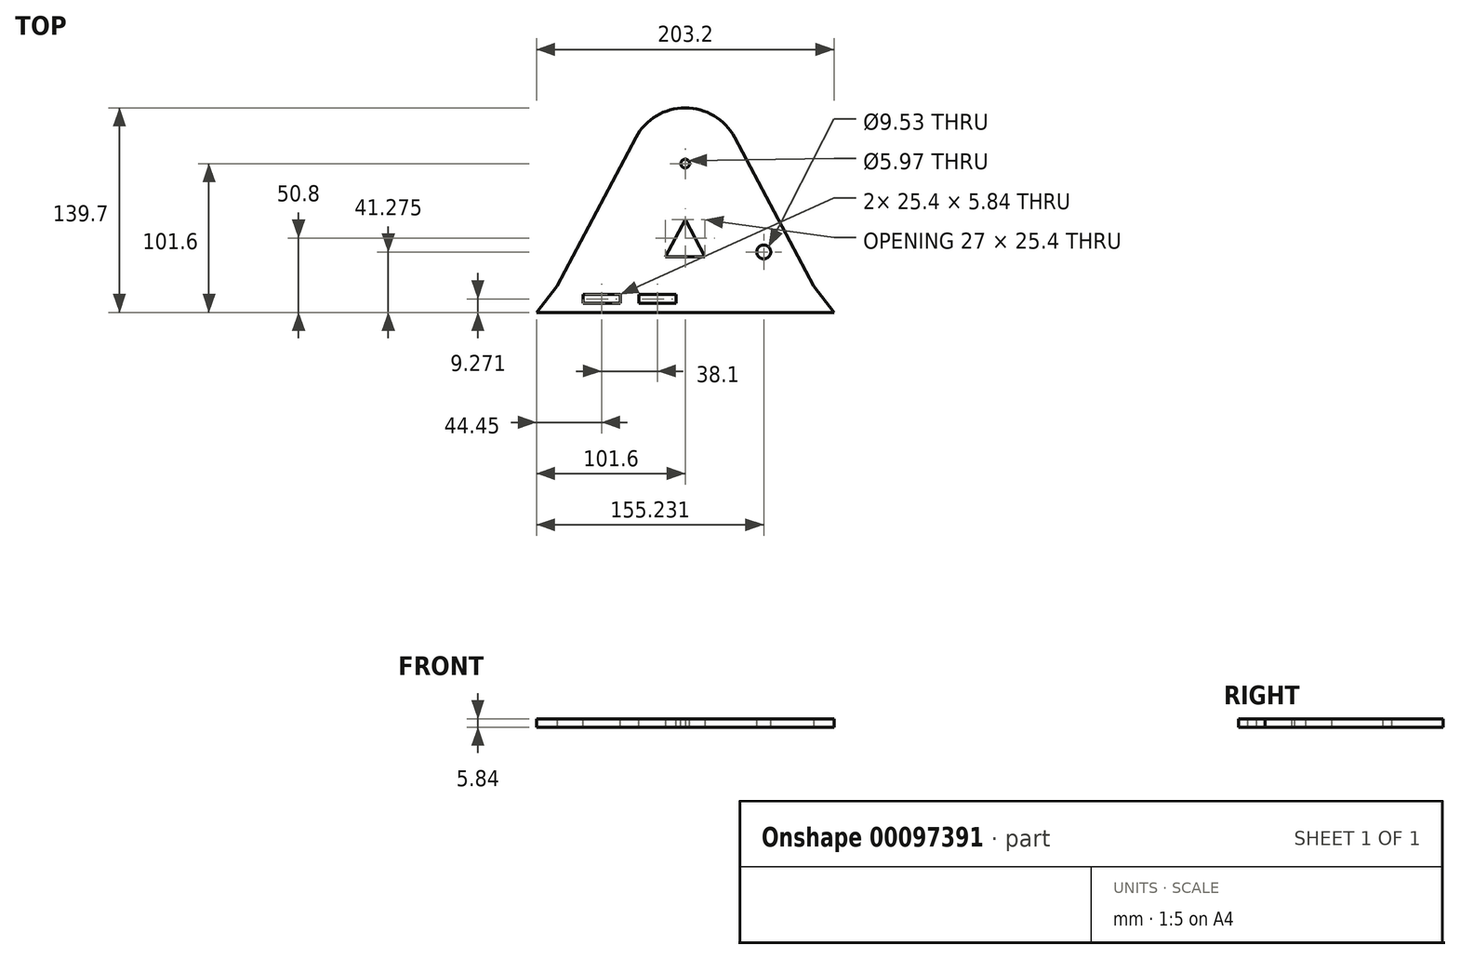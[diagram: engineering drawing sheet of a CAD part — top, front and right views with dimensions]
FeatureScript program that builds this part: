
annotation { "Feature Type Name" : "Feature", "Feature Type Description" : "" }
export const myFeature = defineFeature(function(context is Context, id is Id, definition is map)
    precondition{}
    {
        {
            var Q0;
            Q0=qCreatedBy(makeId("Top.planeOp"),FACE);
            var sketch = newSketch(context, id + "F0", { "sketchPlane" : qUnion([Q0])});
            skCircle(sketch, "E0", {"center": v(0, 0) * mm, "radius": 38.1 * mm});
            skCircle(sketch, "E1", {"center": v(54, -101.6) * mm, "radius": 38.1 * mm, "construction": true});
            skCircle(sketch, "E2", {"center": v(-54, -101.6) * mm, "radius": 38.1 * mm, "construction": true});
            skLineSegment(sketch, "E3", {"start": v(-87.64, -83.72) * mm, "end": v(-33.64, 17.88) * mm});
            skLineSegment(sketch, "E4", {"start": v(87.64, -83.72) * mm, "end": v(33.64, 17.88) * mm});
            skLineSegment(sketch, "E5", {"start": v(0, 0) * mm, "end": v(0, -101.6) * mm, "construction": true});
            skLineSegment(sketch, "E6", {"start": v(-54, -101.6) * mm, "end": v(54, -101.6) * mm, "construction": true});
            skLineSegment(sketch, "E7", {"start": v(-87.64, -83.72) * mm, "end": v(-101.6, -101.6) * mm});
            skLineSegment(sketch, "E8", {"start": v(-54, -101.6) * mm, "end": v(-101.6, -101.6) * mm});
            skLineSegment(sketch, "E9", {"start": v(87.64, -83.72) * mm, "end": v(101.6, -101.6) * mm});
            skLineSegment(sketch, "E10", {"start": v(54, -101.6) * mm, "end": v(101.6, -101.6) * mm});
            skLineSegment(sketch, "E11", {"start": v(0, -38.1) * mm, "end": v(-22.42, -80.28) * mm});
            skLineSegment(sketch, "E12", {"start": v(0, -38.1) * mm, "end": v(22.42, -80.28) * mm});
            skLineSegment(sketch, "E13", {"start": v(-22.42, -80.28) * mm, "end": v(22.42, -80.28) * mm});
            skLineSegment(sketch, "E14", {"start": v(54, -101.6) * mm, "end": v(-54, -101.6) * mm});
            skLineSegment(sketch, "E15", {"start": v(-54, -63.5) * mm, "end": v(54, -63.5) * mm});
            skLineSegment(sketch, "E16", {"start": v(13.5, -63.5) * mm, "end": v(13.5, -101.6) * mm, "construction": true});
            skLineSegment(sketch, "E17", {"start": v(13.5, -63.5) * mm, "end": v(76.9, -63.5) * mm, "construction": true});
            skSolve(sketch);
        }
        {
            var Q0;
            {var subQ0=sQuery(id+"F0.wireOp",EDGE,"E0");var subQ1=makeQuery(id+"F0.imprint","INTERSECT",VERTEX,{"derivedFrom":[subQ0,sQuery(id+"F0.wireOp",EDGE,"E3")]});Q0=makeQuery(id+"F0.imprint","IMPRINT",FACE,{"disambiguationData":[TD([[makeQuery(id+"F0.imprint","IMPRINT",EDGE,{"disambiguationData":[TD([[subQ1,1.0]])],"derivedFrom":subQ0}),1.0]])]});}
            var Q1;
            {var subQ0=sQuery(id+"F0.wireOp",EDGE,"E3");Q1=makeQuery(id+"F0.imprint","IMPRINT",FACE,{"disambiguationData":[TD([[makeQuery(id+"F0.imprint","IMPRINT",EDGE,{"derivedFrom":subQ0}),-1.0]])]});}
            var Q2;
            {var subQ0=sQuery(id+"F0.wireOp",EDGE,"E13");Q2=makeQuery(id+"F0.imprint","IMPRINT",FACE,{"disambiguationData":[TD([[makeQuery(id+"F0.imprint","IMPRINT",EDGE,{"derivedFrom":subQ0}),1.0]])]});}
            extrude(context, id + "F1", {"entities" : qUnion([Q0, Q1, Q2]), "depth" : 5.84 * mm});
        }
        {
            var Q0;
            Q0=makeQuery(id+"F1.opExtrude","CAP_FACE",FACE,{"disambiguationData":[OSD([sQuery(id+"F0.wireOp",EDGE,"E0"),sQuery(id+"F0.wireOp",EDGE,"E3"),sQuery(id+"F0.wireOp",EDGE,"E4"),sQuery(id+"F0.wireOp",EDGE,"E7"),sQuery(id+"F0.wireOp",EDGE,"E8"),sQuery(id+"F0.wireOp",EDGE,"E9"),sQuery(id+"F0.wireOp",EDGE,"E10"),sQuery(id+"F0.wireOp",EDGE,"E11"),sQuery(id+"F0.wireOp",EDGE,"E12"),sQuery(id+"F0.wireOp",EDGE,"E14"),sQuery(id+"F0.wireOp",EDGE,"E15")])],"isStart":false});
            var sketch = newSketch(context, id + "F2", { "sketchPlane" : qUnion([Q0])});
            skCircle(sketch, "E18", {"center": v(0, 0) * mm, "radius": 2.98 * mm});
            skCircle(sketch, "E19", {"center": v(53.63, -60.33) * mm, "radius": 4.76 * mm});
            skLineSegment(sketch, "E20", {"start": v(53.63, -60.33) * mm, "end": v(70.45, -51.39) * mm, "construction": true});
            skSolve(sketch);
        }
        {
            var Q0;
            Q0=makeQuery(id+"F2.imprint","IMPRINT",FACE,{"disambiguationData":[TD([[makeQuery(id+"F2.imprint","IMPRINT",EDGE,{"derivedFrom":sQuery(id+"F2.wireOp",EDGE,"E18")}),1.0]])]});
            var Q1;
            Q1=makeQuery(id+"F2.imprint","IMPRINT",FACE,{"disambiguationData":[TD([[makeQuery(id+"F2.imprint","IMPRINT",EDGE,{"derivedFrom":sQuery(id+"F2.wireOp",EDGE,"E19")}),1.0]])]});
            extrude(context, id + "F3", {"entities" : qUnion([Q0, Q1]), "operationType" : NewBodyOperationType.REMOVE, "oppositeDirection" : true, "depth" : 25.4 * mm});
        }
        {
            var Q0;
            Q0=makeQuery(id+"F1.opExtrude","CAP_FACE",FACE,{"disambiguationData":[OSD([sQuery(id+"F0.wireOp",EDGE,"E0"),sQuery(id+"F0.wireOp",EDGE,"E3"),sQuery(id+"F0.wireOp",EDGE,"E4"),sQuery(id+"F0.wireOp",EDGE,"E7"),sQuery(id+"F0.wireOp",EDGE,"E8"),sQuery(id+"F0.wireOp",EDGE,"E9"),sQuery(id+"F0.wireOp",EDGE,"E10"),sQuery(id+"F0.wireOp",EDGE,"E11"),sQuery(id+"F0.wireOp",EDGE,"E12"),sQuery(id+"F0.wireOp",EDGE,"E14"),sQuery(id+"F0.wireOp",EDGE,"E15")])],"isStart":false});
            var sketch = newSketch(context, id + "F4", { "sketchPlane" : qUnion([Q0])});
            skLineSegment(sketch, "E21.bottom", {"start": v(-6.35, -95.25) * mm, "end": v(-31.75, -95.25) * mm});
            skLineSegment(sketch, "E21.top", {"start": v(-6.35, -89.4) * mm, "end": v(-31.75, -89.4) * mm});
            skLineSegment(sketch, "E21.left", {"start": v(-6.35, -95.25) * mm, "end": v(-6.35, -89.4) * mm});
            skLineSegment(sketch, "E21.right", {"start": v(-31.75, -95.25) * mm, "end": v(-31.75, -89.4) * mm});
            skLineSegment(sketch, "E22.bottom", {"start": v(-44.45, -95.25) * mm, "end": v(-69.85, -95.25) * mm});
            skLineSegment(sketch, "E22.top", {"start": v(-44.45, -89.4) * mm, "end": v(-69.85, -89.4) * mm});
            skLineSegment(sketch, "E22.left", {"start": v(-44.45, -95.25) * mm, "end": v(-44.45, -89.4) * mm});
            skLineSegment(sketch, "E22.right", {"start": v(-69.85, -95.25) * mm, "end": v(-69.85, -89.4) * mm});
            skPoint(sketch, "E23", {"position": v(0, -63.5) * mm});
            skSolve(sketch);
        }
        {
            var Q0;
            Q0=makeQuery(id+"F4.imprint","IMPRINT",FACE,{"disambiguationData":[TD([[makeQuery(id+"F4.imprint","IMPRINT",EDGE,{"derivedFrom":sQuery(id+"F4.wireOp",EDGE,"E22.bottom")}),-1.0]])]});
            var Q1;
            Q1=makeQuery(id+"F4.imprint","IMPRINT",FACE,{"disambiguationData":[TD([[makeQuery(id+"F4.imprint","IMPRINT",EDGE,{"derivedFrom":sQuery(id+"F4.wireOp",EDGE,"E21.bottom")}),-1.0]])]});
            extrude(context, id + "F5", {"entities" : qUnion([Q0, Q1]), "operationType" : NewBodyOperationType.REMOVE, "oppositeDirection" : true, "depth" : 25.4 * mm});
        }
    });
